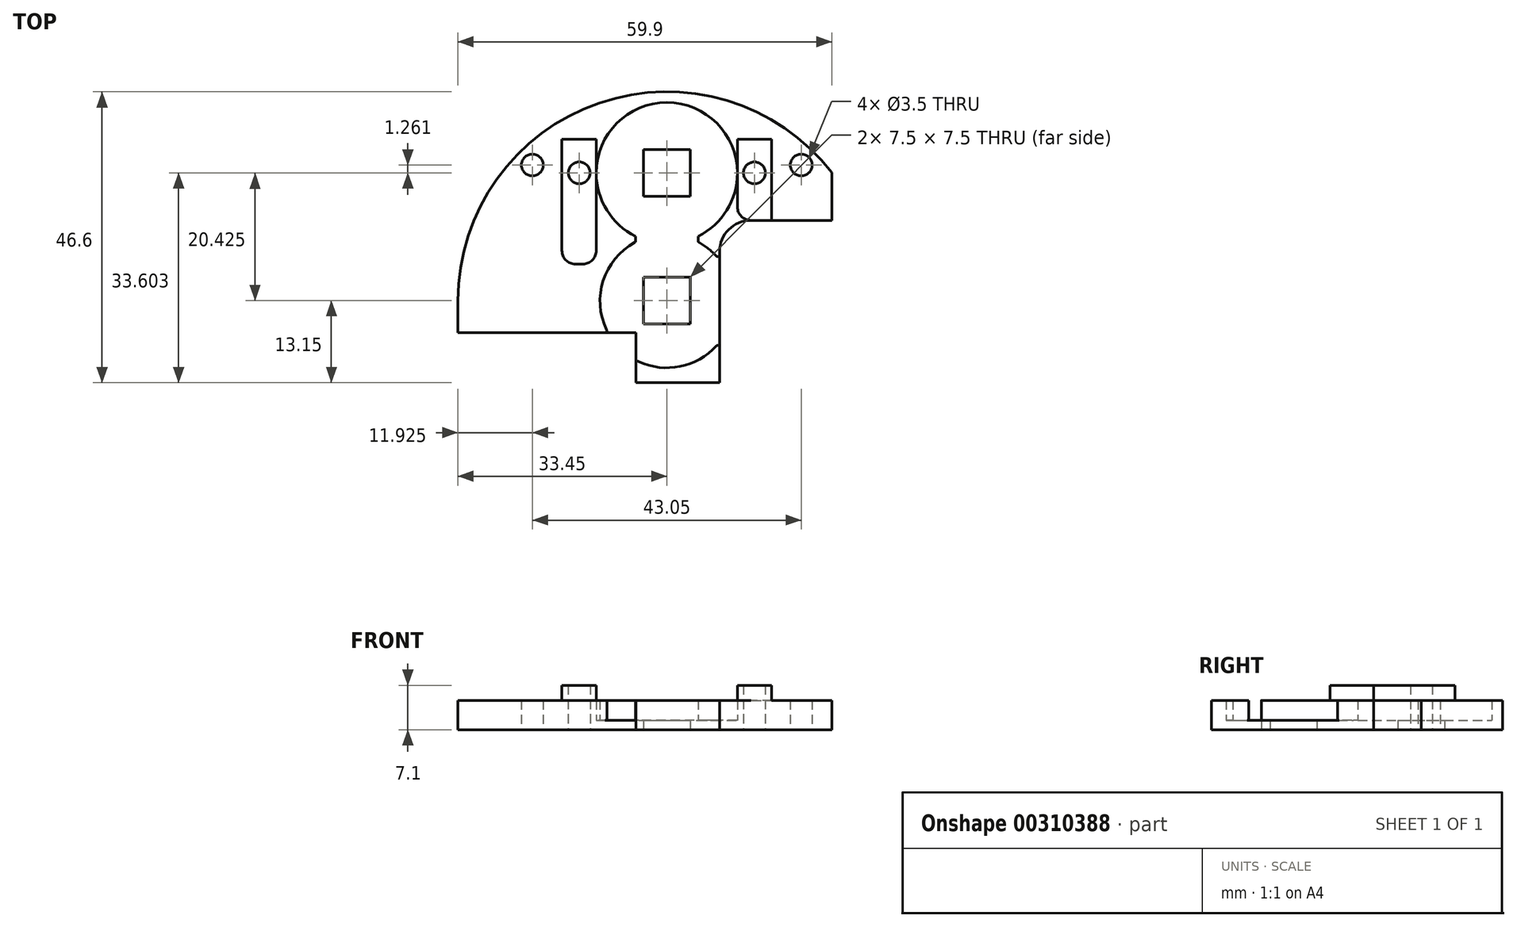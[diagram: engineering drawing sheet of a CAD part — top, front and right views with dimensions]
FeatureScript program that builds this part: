
annotation { "Feature Type Name" : "Feature", "Feature Type Description" : "" }
export const myFeature = defineFeature(function(context is Context, id is Id, definition is map)
    precondition{}
    {
        {
            var Q0;
            Q0=qCreatedBy(makeId("Top.planeOp"),FACE);
            var sketch = newSketch(context, id + "F0", { "sketchPlane" : qUnion([Q0])});
            skLineSegment(sketch, "E0.bottom", {"start": v(-33.45, 25.8) * mm, "end": v(33.45, 25.8) * mm});
            skLineSegment(sketch, "E0.top", {"start": v(-33.45, -25.8) * mm, "end": v(33.45, -25.8) * mm});
            skLineSegment(sketch, "E0.left", {"start": v(-33.45, 25.8) * mm, "end": v(-33.45, -25.8) * mm});
            skLineSegment(sketch, "E0.right", {"start": v(33.45, 25.8) * mm, "end": v(33.45, -25.8) * mm});
            skPoint(sketch, "E0.middle", {"position": v(0, 0) * mm});
            skSolve(sketch);
        }
        {
            var Q0;
            Q0 = qSketchRegion(id + "F0", true);
            extrude(context, id + "F1", {"entities" : qUnion([Q0]), "depth" : 1.5 * mm});
        }
        {
            var Q0;
            Q0=makeQuery(id+"F1.opExtrude","SWEPT_EDGE",EDGE,{"disambiguationData":[OSD([sQuery(id+"F0.wireOp",EDGE,"E0.bottom"),sQuery(id+"F0.wireOp",EDGE,"E0.left")])]});
            var Q1;
            Q1=makeQuery(id+"F1.opExtrude","SWEPT_EDGE",EDGE,{"disambiguationData":[OSD([sQuery(id+"F0.wireOp",EDGE,"E0.bottom"),sQuery(id+"F0.wireOp",EDGE,"E0.right")])]});
            fillet(context, id + "F2", {"entities" : qUnion([Q0, Q1]), "radius" : 33.45 * mm, "tangentPropagation" : true, "allowEdgeOverflow" : false});
        }
        {
            var Q0;
            Q0=qCreatedBy(makeId("Top.planeOp"),FACE);
            var sketch = newSketch(context, id + "F3", { "sketchPlane" : qUnion([Q0])});
            skCircle(sketch, "E1", {"center": v(-21.53, 14.06) * mm, "radius": 1.75 * mm});
            skCircle(sketch, "E2", {"center": v(-14.03, 12.8) * mm, "radius": 1.75 * mm});
            skCircle(sketch, "E3", {"center": v(21.53, 14.06) * mm, "radius": 1.75 * mm});
            skCircle(sketch, "E4", {"center": v(14.02, 12.8) * mm, "radius": 1.75 * mm});
            skSolve(sketch);
        }
        {
            var Q0;
            Q0=qCreatedBy(makeId("Top.planeOp"),FACE);
            var sketch = newSketch(context, id + "F4", { "sketchPlane" : qUnion([Q0])});
            skLineSegment(sketch, "E5.bottom", {"start": v(-2.55, -9.65) * mm, "end": v(2.65, -9.65) * mm});
            skLineSegment(sketch, "E5.top", {"start": v(-2.55, -5.8) * mm, "end": v(2.65, -5.8) * mm});
            skLineSegment(sketch, "E5.left", {"start": v(-2.55, -9.65) * mm, "end": v(-2.55, -5.8) * mm});
            skLineSegment(sketch, "E5.right", {"start": v(2.65, -9.65) * mm, "end": v(2.65, -5.8) * mm});
            skPoint(sketch, "E5.middle", {"position": v(0.05, -7.73) * mm});
            skLineSegment(sketch, "E6.bottom", {"start": v(-2.4, 10.85) * mm, "end": v(2.65, 10.85) * mm});
            skLineSegment(sketch, "E6.top", {"start": v(-2.4, 14.7) * mm, "end": v(2.65, 14.7) * mm});
            skLineSegment(sketch, "E6.left", {"start": v(-2.4, 10.85) * mm, "end": v(-2.4, 14.7) * mm});
            skLineSegment(sketch, "E6.right", {"start": v(2.65, 10.85) * mm, "end": v(2.65, 14.7) * mm});
            skPoint(sketch, "E6.middle", {"position": v(0.12, 12.78) * mm});
            skSolve(sketch);
        }
        {
            var Q0;
            Q0 = qSketchRegion(id + "F3", true);
            extrude(context, id + "F5", {"entities" : qUnion([Q0]), "operationType" : NewBodyOperationType.REMOVE, "depth" : 10 * mm});
        }
        {
            var Q0;
            Q0=makeQuery(id+"F1.opExtrude","SWEPT_FACE",FACE,{"disambiguationData":[OSD([sQuery(id+"F0.wireOp",EDGE,"E0.right")])]});
            var sketch = newSketch(context, id + "F6", { "sketchPlane" : qUnion([Q0])});
            skLineSegment(sketch, "E7.bottom", {"start": v(-25.8, 1.5) * mm, "end": v(34.2, 1.5) * mm});
            skLineSegment(sketch, "E7.top", {"start": v(-25.8, 0) * mm, "end": v(34.2, 0) * mm});
            skLineSegment(sketch, "E7.left", {"start": v(-25.8, 1.5) * mm, "end": v(-25.8, 0) * mm});
            skLineSegment(sketch, "E7.right", {"start": v(34.2, 1.5) * mm, "end": v(34.2, 0) * mm});
            skSolve(sketch);
        }
        {
            var Q0;
            Q0 = qSketchRegion(id + "F6", true);
            extrude(context, id + "F7", {"entities" : qUnion([Q0]), "operationType" : NewBodyOperationType.REMOVE, "oppositeDirection" : true, "depth" : 7 * mm});
        }
        {
            var Q0;
            Q0=makeQuery(id+"F1.opExtrude","SWEPT_FACE",FACE,{"disambiguationData":[OSD([sQuery(id+"F0.wireOp",EDGE,"E0.top")])]});
            var sketch = newSketch(context, id + "F8", { "sketchPlane" : qUnion([Q0])});
            skLineSegment(sketch, "E8.bottom", {"start": v(-33.45, 1.5) * mm, "end": v(-4.95, 1.5) * mm});
            skLineSegment(sketch, "E8.top", {"start": v(-33.45, 0) * mm, "end": v(-4.95, 0) * mm});
            skLineSegment(sketch, "E8.left", {"start": v(-33.45, 1.5) * mm, "end": v(-33.45, 0) * mm});
            skLineSegment(sketch, "E8.right", {"start": v(-4.95, 1.5) * mm, "end": v(-4.95, 0) * mm});
            skSolve(sketch);
        }
        {
            var Q0;
            Q0 = qSketchRegion(id + "F8", true);
            extrude(context, id + "F9", {"entities" : qUnion([Q0]), "operationType" : NewBodyOperationType.REMOVE, "oppositeDirection" : true, "depth" : 13 * mm});
        }
        {
            var Q0;
            Q0=makeQuery(id+"F1.opExtrude","SWEPT_FACE",FACE,{"disambiguationData":[OSD([sQuery(id+"F0.wireOp",EDGE,"E0.top")])]});
            var sketch = newSketch(context, id + "F10", { "sketchPlane" : qUnion([Q0])});
            skLineSegment(sketch, "E9.bottom", {"start": v(26.45, 1.5) * mm, "end": v(8.45, 1.5) * mm});
            skLineSegment(sketch, "E9.top", {"start": v(26.45, 0) * mm, "end": v(8.45, 0) * mm});
            skLineSegment(sketch, "E9.left", {"start": v(26.45, 1.5) * mm, "end": v(26.45, 0) * mm});
            skLineSegment(sketch, "E9.right", {"start": v(8.45, 1.5) * mm, "end": v(8.45, 0) * mm});
            skSolve(sketch);
        }
        {
            var Q0;
            Q0 = qSketchRegion(id + "F10", true);
            extrude(context, id + "F11", {"entities" : qUnion([Q0]), "operationType" : NewBodyOperationType.REMOVE, "oppositeDirection" : true, "depth" : 31 * mm});
        }
        {
            var Q0;
            Q0=makeQuery(id+"F11.boolean.opBoolean","COPY",EDGE,{"derivedFrom":makeQuery(id+"F11.opExtrude","CAP_EDGE",EDGE,{"disambiguationData":[OSD([sQuery(id+"F10.wireOp",EDGE,"E9.right")])],"isStart":false})});
            fillet(context, id + "F12", {"entities" : qUnion([Q0]), "radius" : 5 * mm, "tangentPropagation" : true, "allowEdgeOverflow" : false});
        }
        {
            var Q0;
            Q0=makeQuery(id+"F1.opExtrude","CAP_FACE",FACE,{"disambiguationData":[OSD([sQuery(id+"F0.wireOp",EDGE,"E0.bottom"),sQuery(id+"F0.wireOp",EDGE,"E0.top"),sQuery(id+"F0.wireOp",EDGE,"E0.left"),sQuery(id+"F0.wireOp",EDGE,"E0.right")])],"isStart":false});
            var sketch = newSketch(context, id + "F13", { "sketchPlane" : qUnion([Q0])});
            skCircle(sketch, "E10", {"center": v(0, 12.78) * mm, "radius": 11.3 * mm});
            skSolve(sketch);
        }
        {
            var Q0;
            Q0=makeQuery(id+"F1.opExtrude","CAP_FACE",FACE,{"disambiguationData":[OSD([sQuery(id+"F0.wireOp",EDGE,"E0.bottom"),sQuery(id+"F0.wireOp",EDGE,"E0.top"),sQuery(id+"F0.wireOp",EDGE,"E0.left"),sQuery(id+"F0.wireOp",EDGE,"E0.right")])],"isStart":true});
            var sketch = newSketch(context, id + "F14", { "sketchPlane" : qUnion([Q0])});
            skLineSegment(sketch, "E11.bottom", {"start": v(-3.75, -16.53) * mm, "end": v(3.75, -16.53) * mm});
            skLineSegment(sketch, "E11.top", {"start": v(-3.75, -9.03) * mm, "end": v(3.75, -9.03) * mm});
            skLineSegment(sketch, "E11.left", {"start": v(-3.75, -16.53) * mm, "end": v(-3.75, -9.03) * mm});
            skLineSegment(sketch, "E11.right", {"start": v(3.75, -16.53) * mm, "end": v(3.75, -9.03) * mm});
            skPoint(sketch, "E11.middle", {"position": v(0, -12.78) * mm});
            skLineSegment(sketch, "E12.bottom", {"start": v(3.75, 3.9) * mm, "end": v(-3.75, 3.9) * mm});
            skLineSegment(sketch, "E12.top", {"start": v(3.75, 11.4) * mm, "end": v(-3.75, 11.4) * mm});
            skLineSegment(sketch, "E12.left", {"start": v(3.75, 3.9) * mm, "end": v(3.75, 11.4) * mm});
            skLineSegment(sketch, "E12.right", {"start": v(-3.75, 3.9) * mm, "end": v(-3.75, 11.4) * mm});
            skPoint(sketch, "E12.middle", {"position": v(0, 7.65) * mm});
            skSolve(sketch);
        }
        {
            var Q0;
            Q0=makeQuery(id+"F13.imprint","IMPRINT",FACE,{"disambiguationData":[TD([[makeQuery(id+"F13.imprint","IMPRINT",EDGE,{"derivedFrom":sQuery(id+"F13.wireOp",EDGE,"E10")}),-1.0]])]});
            extrude(context, id + "F15", {"entities" : qUnion([Q0]), "operationType" : NewBodyOperationType.ADD, "depth" : 3.2 * mm});
        }
        {
            var Q0;
            Q0=makeQuery(id+"F13.imprint","IMPRINT",FACE,{"disambiguationData":[TD([[makeQuery(id+"F13.imprint","IMPRINT",EDGE,{"derivedFrom":sQuery(id+"F13.wireOp",EDGE,"E10")}),-1.0]])]});
            var sketch = newSketch(context, id + "F16", { "sketchPlane" : qUnion([Q0])});
            skCircle(sketch, "E13", {"center": v(0, -7.73) * mm, "radius": 10.7 * mm});
            skSolve(sketch);
        }
        {
            var Q0;
            Q0 = qSketchRegion(id + "F16", true);
            extrude(context, id + "F17", {"entities" : qUnion([Q0]), "operationType" : NewBodyOperationType.REMOVE, "depth" : 3.2 * mm});
        }
        {
            var Q0;
            Q0=makeQuery(id+"F17.boolean.opBoolean","MERGE",FACE,{"derivedFrom":[makeQuery(id+"F1.opExtrude","CAP_FACE",FACE,{"disambiguationData":[OSD([sQuery(id+"F0.wireOp",EDGE,"E0.bottom"),sQuery(id+"F0.wireOp",EDGE,"E0.top"),sQuery(id+"F0.wireOp",EDGE,"E0.left"),sQuery(id+"F0.wireOp",EDGE,"E0.right")])],"isStart":false}),makeQuery(id+"F17.opExtrude","CAP_FACE",FACE,{"disambiguationData":[OSD([sQuery(id+"F16.wireOp",EDGE,"E13")])],"isStart":true})]});
            var sketch = newSketch(context, id + "F18", { "sketchPlane" : qUnion([Q0])});
            skLineSegment(sketch, "E14.bottom", {"start": v(-5, 4) * mm, "end": v(5, 4) * mm});
            skLineSegment(sketch, "E14.top", {"start": v(-5, -4) * mm, "end": v(5, -4) * mm});
            skLineSegment(sketch, "E14.left", {"start": v(-5, 4) * mm, "end": v(-5, -4) * mm});
            skLineSegment(sketch, "E14.right", {"start": v(5, 4) * mm, "end": v(5, -4) * mm});
            skPoint(sketch, "E14.middle", {"position": v(0, 0) * mm});
            skSolve(sketch);
        }
        {
            var Q0;
            Q0 = qSketchRegion(id + "F18", true);
            extrude(context, id + "F19", {"entities" : qUnion([Q0]), "operationType" : NewBodyOperationType.REMOVE, "depth" : 5 * mm});
        }
        {
            var Q0;
            Q0 = qSketchRegion(id + "F14", true);
            extrude(context, id + "F20", {"entities" : qUnion([Q0]), "operationType" : NewBodyOperationType.REMOVE, "oppositeDirection" : true, "depth" : 25 * mm});
        }
        {
            var Q0;
            {var subQ0=sQuery(id+"F0.wireOp",EDGE,"E0.top");Q0=makeQuery(id+"F15.boolean.opBoolean","MERGE",FACE,{"derivedFrom":[makeQuery(id+"F1.opExtrude","SWEPT_FACE",FACE,{"disambiguationData":[OSD([subQ0])]}),makeQuery(id+"F15.opExtrude","SWEPT_FACE",FACE,{"disambiguationData":[OSD([subQ0])]})]});}
            var sketch = newSketch(context, id + "F21", { "sketchPlane" : qUnion([Q0])});
            skLineSegment(sketch, "E15.bottom", {"start": v(-4.95, 4.7) * mm, "end": v(8.45, 4.7) * mm});
            skLineSegment(sketch, "E15.top", {"start": v(-4.95, 0) * mm, "end": v(8.45, 0) * mm});
            skLineSegment(sketch, "E15.left", {"start": v(-4.95, 4.7) * mm, "end": v(-4.95, 0) * mm});
            skLineSegment(sketch, "E15.right", {"start": v(8.45, 4.7) * mm, "end": v(8.45, 0) * mm});
            skSolve(sketch);
        }
        {
            var Q0;
            Q0=makeQuery(id+"F21.imprint","IMPRINT",FACE,{"disambiguationData":[TD([[makeQuery(id+"F21.imprint","IMPRINT",EDGE,{"derivedFrom":sQuery(id+"F21.wireOp",EDGE,"E15.bottom")}),-1.0]])]});
            extrude(context, id + "F22", {"entities" : qUnion([Q0]), "operationType" : NewBodyOperationType.REMOVE, "oppositeDirection" : true, "depth" : 5 * mm});
        }
        {
            var Q0;
            {var subQ0=sQuery(id+"F0.wireOp",EDGE,"E0.right");var subQ1=sQuery(id+"F0.wireOp",EDGE,"E0.left");var subQ2=sQuery(id+"F0.wireOp",EDGE,"E0.top");var subQ3=sQuery(id+"F0.wireOp",EDGE,"E0.bottom");var subQ5=makeQuery(id+"F1.opExtrude","SWEPT_FACE",FACE,{"disambiguationData":[OSD([subQ1])]});var subQ6=sQuery(id+"F3.wireOp",EDGE,"84c51ac6-c767-4d04-8e00-3cf61c9bf6e0");var subQ8=sQuery(id+"F8.wireOp",EDGE,"E8.right");var subQ9=sQuery(id+"F8.wireOp",EDGE,"E8.bottom");var subQ12=sQuery(id+"F3.wireOp",EDGE,"E4");var subQ13=sQuery(id+"F3.wireOp",EDGE,"E3");var subQ14=sQuery(id+"F3.wireOp",EDGE,"E2");var subQ15=sQuery(id+"F10.wireOp",EDGE,"E9.right");var subQ18=sQuery(id+"F10.wireOp",EDGE,"E9.bottom");var subQ19=sQuery(id+"F13.wireOp",EDGE,"E10");var subQ20=sQuery(id+"F3.wireOp",EDGE,"E1");var subQ21=sQuery(id+"F6.wireOp",EDGE,"E7.bottom");Q0=makeQuery(id+"F17.boolean.opBoolean","SPLIT",FACE,{"disambiguationData":[TD([subQ5])],"derivedFrom":makeQuery(id+"F15.opExtrude","CAP_FACE",FACE,{"disambiguationData":[OSD([subQ3,subQ2,subQ1,subQ0,subQ20,subQ14,subQ13,subQ12,subQ6,subQ21,subQ9,subQ8,subQ18,subQ15,subQ19])],"isStart":false})});}
            var sketch = newSketch(context, id + "F23", { "sketchPlane" : qUnion([Q0])});
            skLineSegment(sketch, "E16.bottom", {"start": v(-16.8, 18.2) * mm, "end": v(-11.3, 18.2) * mm});
            skLineSegment(sketch, "E16.top", {"start": v(-16.8, -1.8) * mm, "end": v(-11.3, -1.8) * mm});
            skLineSegment(sketch, "E16.left", {"start": v(-16.8, 18.2) * mm, "end": v(-16.8, -1.8) * mm});
            skLineSegment(sketch, "E16.right", {"start": v(-11.3, 18.2) * mm, "end": v(-11.3, -1.8) * mm});
            skLineSegment(sketch, "E17.bottom", {"start": v(11.3, 18.2) * mm, "end": v(16.8, 18.2) * mm});
            skLineSegment(sketch, "E17.top", {"start": v(11.3, 5.2) * mm, "end": v(16.8, 5.2) * mm});
            skLineSegment(sketch, "E17.left", {"start": v(11.3, 18.2) * mm, "end": v(11.3, 5.2) * mm});
            skLineSegment(sketch, "E17.right", {"start": v(16.8, 18.2) * mm, "end": v(16.8, 5.2) * mm});
            skSolve(sketch);
        }
        {
            var Q0;
            Q0 = qSketchRegion(id + "F23", true);
            extrude(context, id + "F24", {"entities" : qUnion([Q0]), "operationType" : NewBodyOperationType.ADD, "depth" : 2.4 * mm});
        }
        {
            var Q0;
            Q0=makeQuery(id+"F1.opExtrude","CAP_FACE",FACE,{"disambiguationData":[OSD([sQuery(id+"F0.wireOp",EDGE,"E0.bottom"),sQuery(id+"F0.wireOp",EDGE,"E0.top"),sQuery(id+"F0.wireOp",EDGE,"E0.left"),sQuery(id+"F0.wireOp",EDGE,"E0.right")])],"isStart":true});
            var sketch = newSketch(context, id + "F25", { "sketchPlane" : qUnion([Q0])});
            skCircle(sketch, "E18", {"center": v(14.02, -12.8) * mm, "radius": 1.75 * mm});
            skCircle(sketch, "E19", {"center": v(-14.03, -12.8) * mm, "radius": 1.75 * mm});
            skSolve(sketch);
        }
        {
            var Q0;
            Q0 = qSketchRegion(id + "F25", true);
            extrude(context, id + "F26", {"entities" : qUnion([Q0]), "operationType" : NewBodyOperationType.REMOVE, "oppositeDirection" : true, "depth" : 25 * mm});
        }
        {
            var Q0;
            Q0=makeQuery(id+"F24.opExtrude","SWEPT_EDGE",EDGE,{"disambiguationData":[OSD([sQuery(id+"F23.wireOp",EDGE,"E17.top"),sQuery(id+"F23.wireOp",EDGE,"E17.left")])]});
            var Q1;
            Q1=makeQuery(id+"F24.opExtrude","SWEPT_EDGE",EDGE,{"disambiguationData":[OSD([sQuery(id+"F23.wireOp",EDGE,"E16.top"),sQuery(id+"F23.wireOp",EDGE,"E16.right")])]});
            var Q2;
            Q2=makeQuery(id+"F24.opExtrude","SWEPT_EDGE",EDGE,{"disambiguationData":[OSD([sQuery(id+"F23.wireOp",EDGE,"E16.top"),sQuery(id+"F23.wireOp",EDGE,"E16.left")])]});
            fillet(context, id + "F27", {"entities" : qUnion([Q0, Q1, Q2]), "radius" : 2.15 * mm, "tangentPropagation" : true, "allowEdgeOverflow" : false});
        }
        {
            var Q0;
            {var subQ0=sQuery(id+"F8.wireOp",EDGE,"E8.bottom");Q0=makeQuery(id+"F17.boolean.opBoolean","INTERSECT",EDGE,{"derivedFrom":[makeQuery(id+"F15.boolean.opBoolean","MERGE",FACE,{"derivedFrom":[makeQuery(id+"F9.boolean.opBoolean","COPY",FACE,{"derivedFrom":makeQuery(id+"F9.opExtrude","CAP_FACE",FACE,{"disambiguationData":[OSD([subQ0,sQuery(id+"F8.wireOp",EDGE,"E8.top"),sQuery(id+"F8.wireOp",EDGE,"E8.left"),sQuery(id+"F8.wireOp",EDGE,"E8.right")])],"isStart":false})}),makeQuery(id+"F15.opExtrude","SWEPT_FACE",FACE,{"disambiguationData":[OSD([subQ0])]})]}),makeQuery(id+"F17.opExtrude","SWEPT_FACE",FACE,{"disambiguationData":[OSD([sQuery(id+"F16.wireOp",EDGE,"E13")])]})]});}
            var Q1;
            {var subQ0=sQuery(id+"F13.wireOp",EDGE,"E10");var subQ1=sQuery(id+"F10.wireOp",EDGE,"E9.right");var subQ2=sQuery(id+"F10.wireOp",EDGE,"E9.bottom");var subQ3=sQuery(id+"F0.wireOp",EDGE,"E0.right");var subQ4=sQuery(id+"F0.wireOp",EDGE,"E0.left");var subQ5=sQuery(id+"F0.wireOp",EDGE,"E0.top");var subQ6=sQuery(id+"F0.wireOp",EDGE,"E0.bottom");var subQ7=sQuery(id+"F16.wireOp",EDGE,"E13");Q1=makeQuery(id+"F19.boolean.opBoolean","INTERSECT",EDGE,{"derivedFrom":[makeQuery(id+"F17.boolean.opBoolean","COPY",FACE,{"disambiguationData":[TD([makeQuery(id+"F1.opExtrude","CAP_FACE",FACE,{"disambiguationData":[OSD([subQ6,subQ5,subQ4,subQ3])],"isStart":false}),makeQuery(id+"F11.boolean.opBoolean","COPY",FACE,{"derivedFrom":makeQuery(id+"F11.opExtrude","SWEPT_FACE",FACE,{"disambiguationData":[OSD([subQ1])]})}),makeQuery(id+"F15.opExtrude","SWEPT_FACE",FACE,{"disambiguationData":[OSD([subQ0])]}),makeQuery(id+"F15.opExtrude","CAP_FACE",FACE,{"disambiguationData":[OSD([subQ6,subQ5,subQ4,subQ3,sQuery(id+"F3.wireOp",EDGE,"E1"),sQuery(id+"F3.wireOp",EDGE,"E2"),sQuery(id+"F3.wireOp",EDGE,"E3"),sQuery(id+"F3.wireOp",EDGE,"E4"),sQuery(id+"F6.wireOp",EDGE,"E7.bottom"),sQuery(id+"F8.wireOp",EDGE,"E8.bottom"),sQuery(id+"F8.wireOp",EDGE,"E8.right"),subQ2,subQ1,subQ0])],"isStart":false}),makeQuery(id+"F15.opExtrude","SWEPT_FACE",FACE,{"disambiguationData":[OSD([subQ5,subQ2,subQ1])]}),makeQuery(id+"F17.opExtrude","CAP_FACE",FACE,{"disambiguationData":[OSD([subQ7])],"isStart":true})])],"derivedFrom":makeQuery(id+"F17.opExtrude","SWEPT_FACE",FACE,{"disambiguationData":[OSD([subQ7])]})}),makeQuery(id+"F19.opExtrude","SWEPT_FACE",FACE,{"disambiguationData":[OSD([sQuery(id+"F18.wireOp",EDGE,"E14.right")])]})]});}
            var Q2;
            {var subQ0=sQuery(id+"F10.wireOp",EDGE,"E9.right");Q2=makeQuery(id+"F17.boolean.opBoolean","INTERSECT",EDGE,{"disambiguationData":[OD(0.0)],"derivedFrom":[makeQuery(id+"F15.boolean.opBoolean","MERGE",FACE,{"derivedFrom":[makeQuery(id+"F11.boolean.opBoolean","COPY",FACE,{"derivedFrom":makeQuery(id+"F11.opExtrude","SWEPT_FACE",FACE,{"disambiguationData":[OSD([subQ0])]})}),makeQuery(id+"F15.opExtrude","SWEPT_FACE",FACE,{"disambiguationData":[OSD([sQuery(id+"F0.wireOp",EDGE,"E0.top"),sQuery(id+"F10.wireOp",EDGE,"E9.bottom"),subQ0])]})]}),makeQuery(id+"F17.opExtrude","SWEPT_FACE",FACE,{"disambiguationData":[OSD([sQuery(id+"F16.wireOp",EDGE,"E13")])]})]});}
            var Q3;
            {var subQ0=sQuery(id+"F10.wireOp",EDGE,"E9.right");Q3=makeQuery(id+"F17.boolean.opBoolean","INTERSECT",EDGE,{"disambiguationData":[OD(1.0)],"derivedFrom":[makeQuery(id+"F15.boolean.opBoolean","MERGE",FACE,{"derivedFrom":[makeQuery(id+"F11.boolean.opBoolean","COPY",FACE,{"derivedFrom":makeQuery(id+"F11.opExtrude","SWEPT_FACE",FACE,{"disambiguationData":[OSD([subQ0])]})}),makeQuery(id+"F15.opExtrude","SWEPT_FACE",FACE,{"disambiguationData":[OSD([sQuery(id+"F0.wireOp",EDGE,"E0.top"),sQuery(id+"F10.wireOp",EDGE,"E9.bottom"),subQ0])]})]}),makeQuery(id+"F17.opExtrude","SWEPT_FACE",FACE,{"disambiguationData":[OSD([sQuery(id+"F16.wireOp",EDGE,"E13")])]})]});}
            var Q4;
            {var subQ0=sQuery(id+"F8.wireOp",EDGE,"E8.right");Q4=makeQuery(id+"F17.boolean.opBoolean","INTERSECT",EDGE,{"derivedFrom":[makeQuery(id+"F15.boolean.opBoolean","MERGE",FACE,{"derivedFrom":[makeQuery(id+"F9.boolean.opBoolean","COPY",FACE,{"derivedFrom":makeQuery(id+"F9.opExtrude","SWEPT_FACE",FACE,{"disambiguationData":[OSD([subQ0])]})}),makeQuery(id+"F15.opExtrude","SWEPT_FACE",FACE,{"disambiguationData":[OSD([sQuery(id+"F0.wireOp",EDGE,"E0.top"),sQuery(id+"F8.wireOp",EDGE,"E8.bottom"),subQ0])]})]}),makeQuery(id+"F17.opExtrude","SWEPT_FACE",FACE,{"disambiguationData":[OSD([sQuery(id+"F16.wireOp",EDGE,"E13")])]})]});}
            var Q5;
            {var subQ0=sQuery(id+"F13.wireOp",EDGE,"E10");var subQ1=sQuery(id+"F8.wireOp",EDGE,"E8.right");var subQ2=sQuery(id+"F8.wireOp",EDGE,"E8.bottom");var subQ3=sQuery(id+"F0.wireOp",EDGE,"E0.right");var subQ4=sQuery(id+"F0.wireOp",EDGE,"E0.left");var subQ5=sQuery(id+"F0.wireOp",EDGE,"E0.top");var subQ6=sQuery(id+"F0.wireOp",EDGE,"E0.bottom");var subQ7=sQuery(id+"F16.wireOp",EDGE,"E13");Q5=makeQuery(id+"F19.boolean.opBoolean","INTERSECT",EDGE,{"derivedFrom":[makeQuery(id+"F17.boolean.opBoolean","COPY",FACE,{"disambiguationData":[TD([makeQuery(id+"F1.opExtrude","CAP_FACE",FACE,{"disambiguationData":[OSD([subQ6,subQ5,subQ4,subQ3])],"isStart":false}),makeQuery(id+"F9.boolean.opBoolean","COPY",FACE,{"derivedFrom":makeQuery(id+"F9.opExtrude","CAP_FACE",FACE,{"disambiguationData":[OSD([subQ2,sQuery(id+"F8.wireOp",EDGE,"E8.top"),sQuery(id+"F8.wireOp",EDGE,"E8.left"),subQ1])],"isStart":false})}),makeQuery(id+"F15.opExtrude","SWEPT_FACE",FACE,{"disambiguationData":[OSD([subQ0])]}),makeQuery(id+"F15.opExtrude","CAP_FACE",FACE,{"disambiguationData":[OSD([subQ6,subQ5,subQ4,subQ3,sQuery(id+"F3.wireOp",EDGE,"E1"),sQuery(id+"F3.wireOp",EDGE,"E2"),sQuery(id+"F3.wireOp",EDGE,"E3"),sQuery(id+"F3.wireOp",EDGE,"E4"),sQuery(id+"F6.wireOp",EDGE,"E7.bottom"),subQ2,subQ1,sQuery(id+"F10.wireOp",EDGE,"E9.bottom"),sQuery(id+"F10.wireOp",EDGE,"E9.right"),subQ0])],"isStart":false}),makeQuery(id+"F15.opExtrude","SWEPT_FACE",FACE,{"disambiguationData":[OSD([subQ2])]}),makeQuery(id+"F17.opExtrude","CAP_FACE",FACE,{"disambiguationData":[OSD([subQ7])],"isStart":true})])],"derivedFrom":makeQuery(id+"F17.opExtrude","SWEPT_FACE",FACE,{"disambiguationData":[OSD([subQ7])]})}),makeQuery(id+"F19.opExtrude","SWEPT_FACE",FACE,{"disambiguationData":[OSD([sQuery(id+"F18.wireOp",EDGE,"E14.left")])]})]});}
            fillet(context, id + "F28", {"entities" : qUnion([Q0, Q1, Q2, Q3, Q4, Q5]), "radius" : 0.3 * mm, "tangentPropagation" : true, "allowEdgeOverflow" : false});
        }
    });
